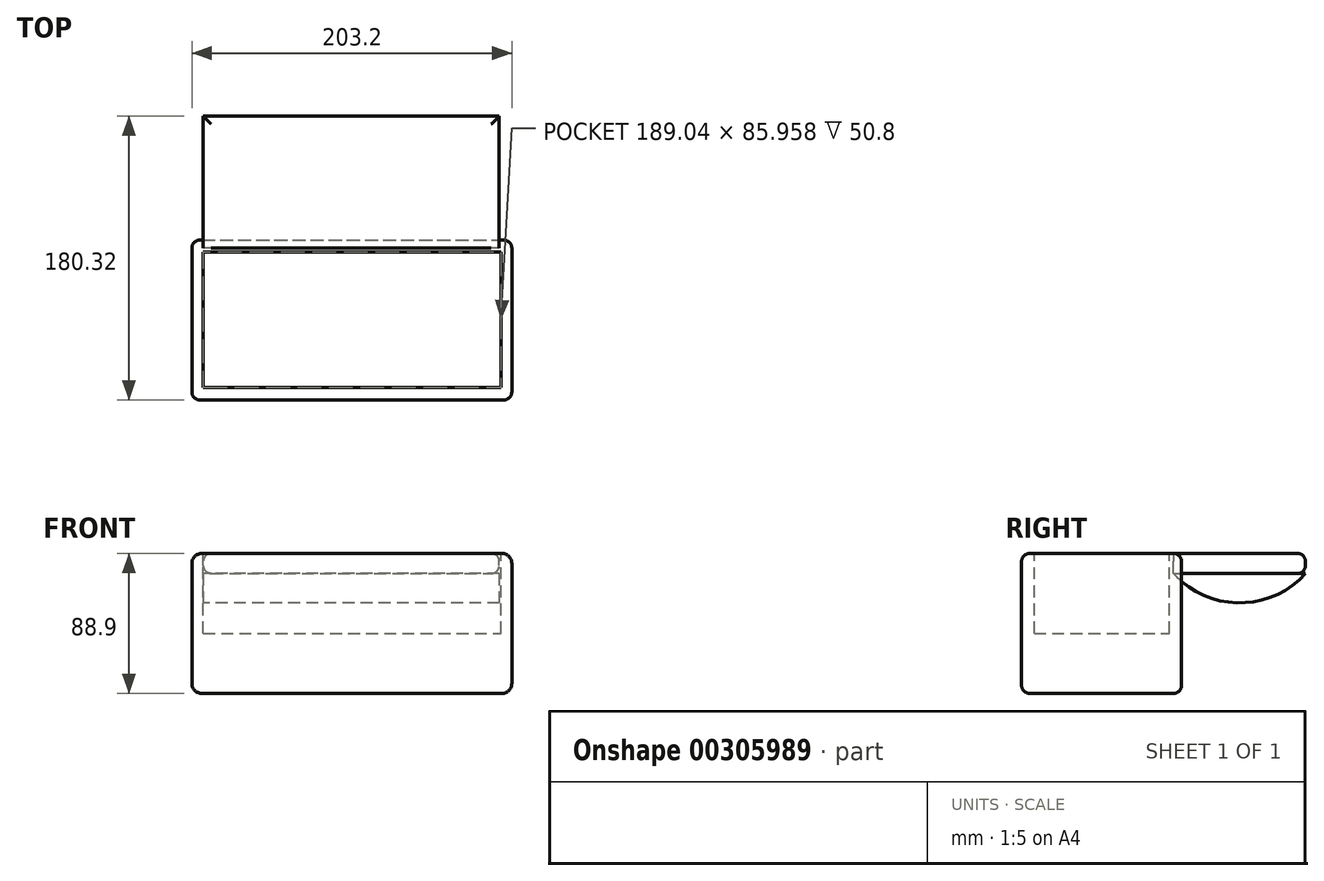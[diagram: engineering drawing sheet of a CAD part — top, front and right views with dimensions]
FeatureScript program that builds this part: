
annotation { "Feature Type Name" : "Feature", "Feature Type Description" : "" }
export const myFeature = defineFeature(function(context is Context, id is Id, definition is map)
    precondition{}
    {
        {
            var Q0;
            Q0=qCreatedBy(makeId("Front.planeOp"),FACE);
            var sketch = newSketch(context, id + "F0", { "sketchPlane" : qUnion([Q0])});
            skLineSegment(sketch, "E0.bottom", {"start": v(-78.27, -39.11) * mm, "end": v(112.23, -39.11) * mm});
            skLineSegment(sketch, "E0.top", {"start": v(-78.27, 49.79) * mm, "end": v(112.23, 49.79) * mm});
            skLineSegment(sketch, "E0.left", {"start": v(-84.62, -32.76) * mm, "end": v(-84.62, 43.44) * mm});
            skLineSegment(sketch, "E0.right", {"start": v(118.58, -32.76) * mm, "end": v(118.58, 43.44) * mm});
            skPoint(sketch, "E1.visualSharp", {"position": v(-84.62, 49.79) * mm});
            skArc(sketch, "E1.filletArc", {"start": v(-78.27, 49.79) * mm, "mid": v(-82.76, 47.93) * mm, "end": v(-84.62, 43.44) * mm});
            skPoint(sketch, "E2.visualSharp", {"position": v(118.58, 49.79) * mm});
            skArc(sketch, "E2.filletArc", {"start": v(118.58, 43.44) * mm, "mid": v(116.72, 47.93) * mm, "end": v(112.23, 49.79) * mm});
            skPoint(sketch, "E3.visualSharp", {"position": v(-84.62, -39.11) * mm});
            skArc(sketch, "E3.filletArc", {"start": v(-84.62, -32.76) * mm, "mid": v(-82.76, -37.25) * mm, "end": v(-78.27, -39.11) * mm});
            skPoint(sketch, "E4.visualSharp", {"position": v(118.58, -39.11) * mm});
            skArc(sketch, "E4.filletArc", {"start": v(112.23, -39.11) * mm, "mid": v(116.72, -37.25) * mm, "end": v(118.58, -32.76) * mm});
            skSolve(sketch);
        }
        {
            var Q0;
            Q0=makeQuery(id+"F0.imprint","IMPRINT",FACE,{"disambiguationData":[TD([[makeQuery(id+"F0.imprint","IMPRINT",EDGE,{"derivedFrom":sQuery(id+"F0.wireOp",EDGE,"E0.bottom")}),1.0]])]});
            extrude(context, id + "F1", {"entities" : qUnion([Q0]), "oppositeDirection" : true, "depth" : 101.6 * mm});
        }
        {
            var Q0;
            Q0=makeQuery(id+"F1.opExtrude","SWEPT_FACE",FACE,{"disambiguationData":[OSD([sQuery(id+"F0.wireOp",EDGE,"E0.top")])]});
            var sketch = newSketch(context, id + "F2", { "sketchPlane" : qUnion([Q0])});
            skLineSegment(sketch, "E5.bottom", {"start": v(-77.37, 8) * mm, "end": v(111.67, 8) * mm});
            skLineSegment(sketch, "E5.top", {"start": v(-77.37, 93.96) * mm, "end": v(111.67, 93.96) * mm});
            skLineSegment(sketch, "E5.left", {"start": v(-77.37, 8) * mm, "end": v(-77.37, 93.96) * mm});
            skLineSegment(sketch, "E5.right", {"start": v(111.67, 8) * mm, "end": v(111.67, 93.96) * mm});
            skSolve(sketch);
        }
        {
            var Q0;
            Q0=makeQuery(id+"F2.imprint","IMPRINT",FACE,{"disambiguationData":[TD([[makeQuery(id+"F2.imprint","IMPRINT",EDGE,{"derivedFrom":sQuery(id+"F2.wireOp",EDGE,"E5.bottom")}),1.0]])]});
            extrude(context, id + "F3", {"entities" : qUnion([Q0]), "operationType" : NewBodyOperationType.REMOVE, "oppositeDirection" : true, "depth" : 50.8 * mm});
        }
        {
            var Q0;
            Q0=makeQuery(id+"F1.opExtrude","CAP_EDGE",EDGE,{"disambiguationData":[OSD([sQuery(id+"F0.wireOp",EDGE,"E0.top")])],"isStart":false});
            var Q1;
            Q1=makeQuery(id+"F1.opExtrude","CAP_EDGE",EDGE,{"disambiguationData":[OSD([sQuery(id+"F0.wireOp",EDGE,"E0.top")])],"isStart":true});
            fillet(context, id + "F4", {"entities" : qUnion([Q0, Q1]), "radius" : 5.08 * mm, "tangentPropagation" : true, "allowEdgeOverflow" : false});
        }
        {
            var Q0;
            Q0=makeQuery(id+"F1.opExtrude","SWEPT_FACE",FACE,{"disambiguationData":[OSD([sQuery(id+"F0.wireOp",EDGE,"E0.top")])]});
            var sketch = newSketch(context, id + "F5", { "sketchPlane" : qUnion([Q0])});
            skLineSegment(sketch, "E6.bottom", {"start": v(-77.37, 93.96) * mm, "end": v(110.59, 93.96) * mm});
            skLineSegment(sketch, "E6.top", {"start": v(-77.37, 180.32) * mm, "end": v(110.59, 180.32) * mm});
            skLineSegment(sketch, "E6.left", {"start": v(-77.37, 93.96) * mm, "end": v(-77.37, 180.32) * mm});
            skLineSegment(sketch, "E6.right", {"start": v(110.59, 93.96) * mm, "end": v(110.59, 180.32) * mm});
            skSolve(sketch);
        }
        {
            var Q0;
            {var subQ0=sQuery(id+"F5.wireOp",EDGE,"E6.top");Q0=makeQuery(id+"F5.imprint","IMPRINT",FACE,{"disambiguationData":[TD([[makeQuery(id+"F5.imprint","IMPRINT",EDGE,{"derivedFrom":subQ0}),-1.0]])]});}
            extrude(context, id + "F6", {"entities" : qUnion([Q0]), "oppositeDirection" : true, "depth" : 12.7 * mm});
        }
        {
            var Q0;
            Q0=makeQuery(id+"F6.opExtrude","SWEPT_FACE",FACE,{"disambiguationData":[OSD([sQuery(id+"F5.wireOp",EDGE,"E6.left")])]});
            var sketch = newSketch(context, id + "F7", { "sketchPlane" : qUnion([Q0])});
            skArc(sketch, "E7", {"start": v(-180.32, 37.09) * mm, "mid": v(-138.42, 18.41) * mm, "end": v(-96.52, 37.09) * mm});
            skSolve(sketch);
        }
        {
            var Q0;
            Q0=makeQuery(id+"F7.imprint","IMPRINT",FACE,{"disambiguationData":[TD([[makeQuery(id+"F7.imprint","IMPRINT",EDGE,{"derivedFrom":sQuery(id+"F7.wireOp",EDGE,"E7")}),1.0]])]});
            extrude(context, id + "F8", {"entities" : qUnion([Q0]), "oppositeDirection" : true, "depth" : 187.96 * mm});
        }
        {
            var Q0;
            Q0=makeQuery(id+"F6.opExtrude","CAP_EDGE",EDGE,{"disambiguationData":[OSD([sQuery(id+"F5.wireOp",EDGE,"E6.left")])],"isStart":true});
            var Q1;
            Q1=makeQuery(id+"F6.opExtrude","CAP_EDGE",EDGE,{"disambiguationData":[OSD([sQuery(id+"F5.wireOp",EDGE,"E6.top")])],"isStart":true});
            var Q2;
            Q2=makeQuery(id+"F6.opExtrude","CAP_EDGE",EDGE,{"disambiguationData":[OSD([sQuery(id+"F5.wireOp",EDGE,"E6.right")])],"isStart":true});
            var Q3;
            Q3=makeQuery(id+"F6.opExtrude","CAP_EDGE",EDGE,{"disambiguationData":[OSD([sQuery(id+"F5.wireOp",EDGE,"E6.top")])],"isStart":false});
            var Q4;
            Q4=makeQuery(id+"F6.opExtrude","CAP_EDGE",EDGE,{"disambiguationData":[OSD([sQuery(id+"F5.wireOp",EDGE,"E6.right")])],"isStart":false});
            var Q5;
            Q5=makeQuery(id+"F6.opExtrude","CAP_EDGE",EDGE,{"disambiguationData":[OSD([sQuery(id+"F5.wireOp",EDGE,"E6.left")])],"isStart":false});
            fillet(context, id + "F9", {"entities" : qUnion([Q0, Q1, Q2, Q3, Q4, Q5]), "radius" : 5.08 * mm, "tangentPropagation" : true, "allowEdgeOverflow" : false});
        }
    });
